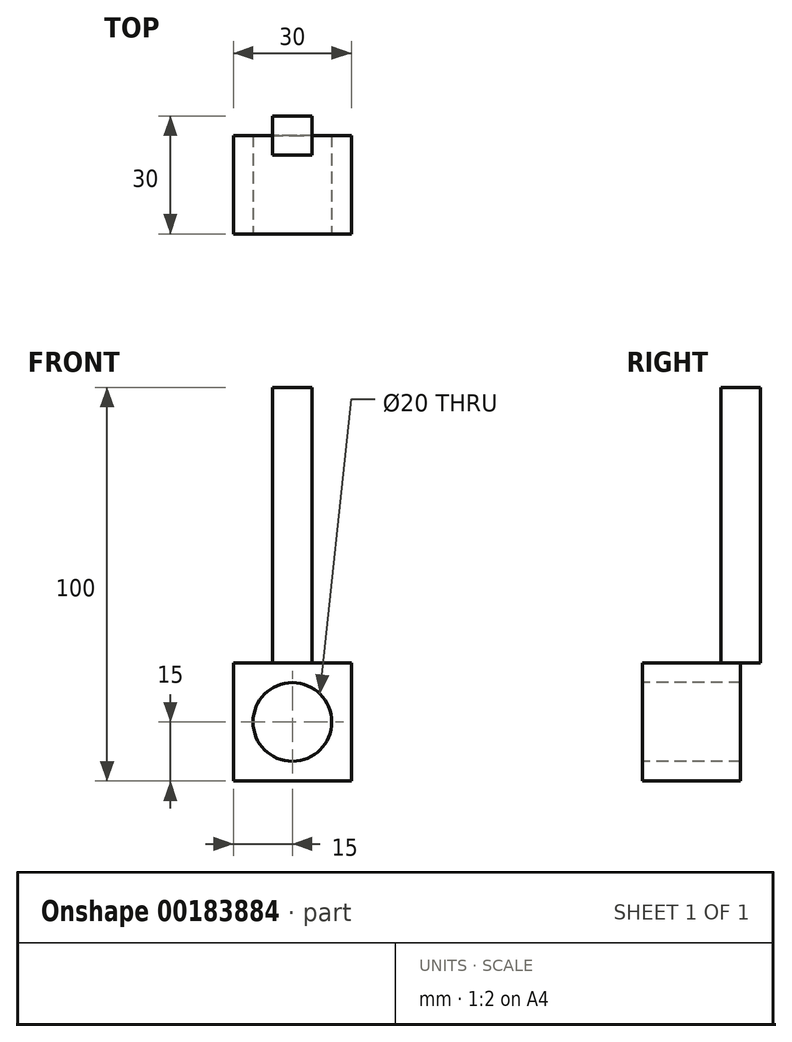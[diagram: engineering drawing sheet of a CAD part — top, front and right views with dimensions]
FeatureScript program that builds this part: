
annotation { "Feature Type Name" : "Feature", "Feature Type Description" : "" }
export const myFeature = defineFeature(function(context is Context, id is Id, definition is map)
    precondition{}
    {
        {
            var Q0;
            Q0=qCreatedBy(makeId("Front.planeOp"),FACE);
            var sketch = newSketch(context, id + "F0", { "sketchPlane" : qUnion([Q0])});
            skLineSegment(sketch, "E0.bottom", {"start": v(15, 15) * mm, "end": v(-15, 15) * mm});
            skLineSegment(sketch, "E0.top", {"start": v(15, -15) * mm, "end": v(-15, -15) * mm});
            skLineSegment(sketch, "E0.left", {"start": v(15, 15) * mm, "end": v(15, -15) * mm});
            skLineSegment(sketch, "E0.right", {"start": v(-15, 15) * mm, "end": v(-15, -15) * mm});
            skPoint(sketch, "E0.middle", {"position": v(0, 0) * mm});
            skSolve(sketch);
        }
        {
            var Q0;
            Q0 = qSketchRegion(id + "F0", true);
            extrude(context, id + "F1", {"entities" : qUnion([Q0]), "depth" : 25 * mm});
        }
        {
            var Q0;
            Q0=makeQuery(id+"F1.opExtrude","CAP_FACE",FACE,{"disambiguationData":[OSD([sQuery(id+"F0.wireOp",EDGE,"E0.bottom"),sQuery(id+"F0.wireOp",EDGE,"E0.top"),sQuery(id+"F0.wireOp",EDGE,"E0.left"),sQuery(id+"F0.wireOp",EDGE,"E0.right")])],"isStart":false});
            var sketch = newSketch(context, id + "F2", { "sketchPlane" : qUnion([Q0])});
            skCircle(sketch, "E1", {"center": v(0, 0) * mm, "radius": 10 * mm});
            skSolve(sketch);
        }
        {
            var Q0;
            Q0 = qSketchRegion(id + "F2", true);
            extrude(context, id + "F3", {"entities" : qUnion([Q0]), "operationType" : NewBodyOperationType.REMOVE, "oppositeDirection" : true, "depth" : 25 * mm});
        }
        {
            var Q0;
            Q0=makeQuery(id+"F1.opExtrude","SWEPT_FACE",FACE,{"disambiguationData":[OSD([sQuery(id+"F0.wireOp",EDGE,"E0.bottom")])]});
            var sketch = newSketch(context, id + "F4", { "sketchPlane" : qUnion([Q0])});
            skLineSegment(sketch, "E2.bottom", {"start": v(-5, -5) * mm, "end": v(5, -5) * mm});
            skLineSegment(sketch, "E2.top", {"start": v(-5, 5) * mm, "end": v(5, 5) * mm});
            skLineSegment(sketch, "E2.left", {"start": v(-5, -5) * mm, "end": v(-5, 5) * mm});
            skLineSegment(sketch, "E2.right", {"start": v(5, -5) * mm, "end": v(5, 5) * mm});
            skPoint(sketch, "E2.middle", {"position": v(0, 0) * mm});
            skSolve(sketch);
        }
        {
            var Q0;
            Q0 = qSketchRegion(id + "F4", true);
            extrude(context, id + "F5", {"entities" : qUnion([Q0]), "operationType" : NewBodyOperationType.ADD, "depth" : 70 * mm});
        }
    });
